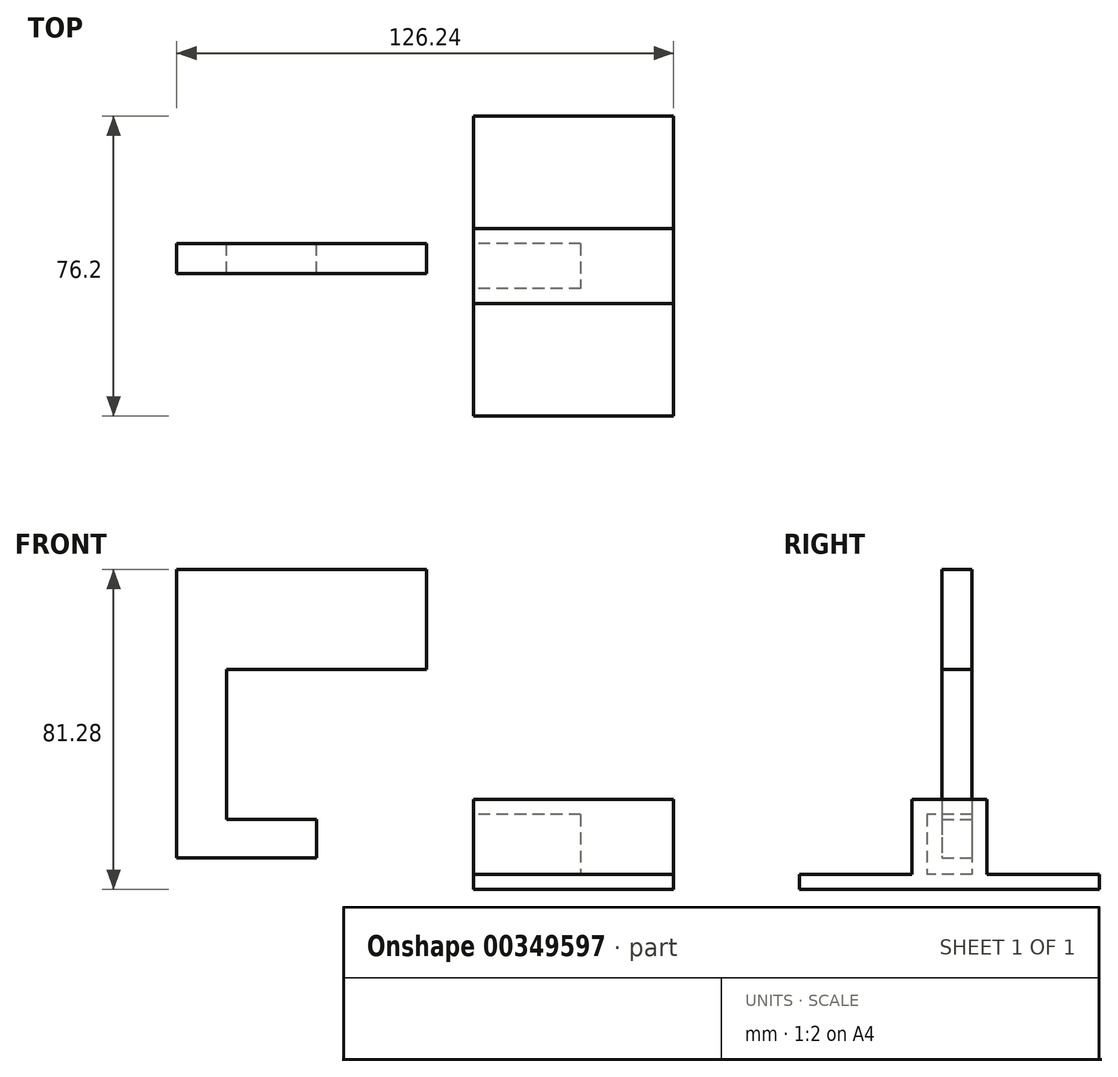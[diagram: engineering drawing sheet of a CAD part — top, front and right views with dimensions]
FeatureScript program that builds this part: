
annotation { "Feature Type Name" : "Feature", "Feature Type Description" : "" }
export const myFeature = defineFeature(function(context is Context, id is Id, definition is map)
    precondition{}
    {
        {
            var Q0;
            Q0=qCreatedBy(makeId("Top.planeOp"),FACE);
            var sketch = newSketch(context, id + "F0", { "sketchPlane" : qUnion([Q0])});
            skLineSegment(sketch, "E0.bottom", {"start": v(-61.72, 63.22) * mm, "end": v(-10.92, 63.22) * mm});
            skLineSegment(sketch, "E0.top", {"start": v(-61.72, -12.98) * mm, "end": v(-10.92, -12.98) * mm});
            skLineSegment(sketch, "E0.left", {"start": v(-61.72, 63.22) * mm, "end": v(-61.72, -12.98) * mm});
            skLineSegment(sketch, "E0.right", {"start": v(-10.92, 63.22) * mm, "end": v(-10.92, -12.98) * mm});
            skSolve(sketch);
        }
        {
            var Q0;
            Q0=makeQuery(id+"F0.imprint","IMPRINT",FACE,{"disambiguationData":[TD([[makeQuery(id+"F0.imprint","IMPRINT",EDGE,{"derivedFrom":sQuery(id+"F0.wireOp",EDGE,"E0.bottom")}),-1.0]])]});
            extrude(context, id + "F1", {"entities" : qUnion([Q0]), "depth" : 3.8 * mm, "offsetDistance" : 25.4 * mm});
        }
        {
            var Q0;
            Q0=makeQuery(id+"F1.opExtrude","CAP_FACE",FACE,{"disambiguationData":[OSD([sQuery(id+"F0.wireOp",EDGE,"E0.bottom"),sQuery(id+"F0.wireOp",EDGE,"E0.top"),sQuery(id+"F0.wireOp",EDGE,"E0.left"),sQuery(id+"F0.wireOp",EDGE,"E0.right")])],"isStart":false});
            var sketch = newSketch(context, id + "F2", { "sketchPlane" : qUnion([Q0])});
            skPoint(sketch, "E1", {"position": v(-61.72, 44.17) * mm});
            skPoint(sketch, "E2", {"position": v(-61.72, 6.07) * mm});
            skPoint(sketch, "E3", {"position": v(-10.92, 15.6) * mm});
            skPoint(sketch, "E4", {"position": v(-10.92, 34.64) * mm});
            skPoint(sketch, "E5", {"position": v(-61.72, 25.12) * mm});
            skPoint(sketch, "E6", {"position": v(-61.72, 34.64) * mm});
            skPoint(sketch, "E7", {"position": v(-61.72, 15.6) * mm});
            skLineSegment(sketch, "E8", {"start": v(-61.72, 34.64) * mm, "end": v(-10.92, 34.64) * mm});
            skLineSegment(sketch, "E9", {"start": v(-61.72, 15.6) * mm, "end": v(-10.92, 15.6) * mm});
            skLineSegment(sketch, "E10", {"start": v(-61.72, 34.64) * mm, "end": v(-61.72, 15.6) * mm});
            skLineSegment(sketch, "E11", {"start": v(-10.92, 34.64) * mm, "end": v(-10.92, 15.6) * mm});
            skSolve(sketch);
        }
        {
            var Q0;
            Q0=makeQuery(id+"F2.imprint","IMPRINT",FACE,{"disambiguationData":[TD([[makeQuery(id+"F2.imprint","IMPRINT",EDGE,{"derivedFrom":sQuery(id+"F2.wireOp",EDGE,"E8")}),-1.0]])]});
            extrude(context, id + "F3", {"entities" : qUnion([Q0]), "operationType" : NewBodyOperationType.ADD, "depth" : 19.05 * mm, "offsetDistance" : 25.4 * mm});
        }
        {
            var Q0;
            Q0=makeQuery(id+"F3.boolean.opBoolean","MERGE",FACE,{"derivedFrom":[makeQuery(id+"F1.opExtrude","SWEPT_FACE",FACE,{"disambiguationData":[OSD([sQuery(id+"F0.wireOp",EDGE,"E0.left")])]}),makeQuery(id+"F3.opExtrude","SWEPT_FACE",FACE,{"disambiguationData":[OSD([sQuery(id+"F2.wireOp",EDGE,"E10")])]})]});
            var sketch = newSketch(context, id + "F4", { "sketchPlane" : qUnion([Q0])});
            skPoint(sketch, "E12", {"position": v(-30.83, 22.86) * mm});
            skPoint(sketch, "E13", {"position": v(-19.4, 22.86) * mm});
            skPoint(sketch, "E14", {"position": v(-15.6, 7.62) * mm});
            skPoint(sketch, "E15", {"position": v(-34.64, 7.62) * mm});
            skLineSegment(sketch, "E16", {"start": v(-34.64, 3.81) * mm, "end": v(-15.6, 3.81) * mm});
            skLineSegment(sketch, "E17", {"start": v(-30.83, 22.86) * mm, "end": v(-30.83, 0) * mm});
            skLineSegment(sketch, "E18", {"start": v(-19.4, 22.86) * mm, "end": v(-19.4, 0) * mm});
            skPoint(sketch, "E19", {"position": v(-34.64, 19.05) * mm});
            skLineSegment(sketch, "E20", {"start": v(-34.64, 19.05) * mm, "end": v(-15.6, 19.05) * mm});
            skSolve(sketch);
        }
        {
            var Q0;
            {var subQ0=sQuery(id+"F4.wireOp",EDGE,"E20");var subQ1=sQuery(id+"F4.wireOp",EDGE,"E17");var subQ2=makeQuery(id+"F4.imprint","INTERSECT",VERTEX,{"derivedFrom":[subQ1,subQ0]});Q0=makeQuery(id+"F4.imprint","IMPRINT",FACE,{"disambiguationData":[TD([[makeQuery(id+"F4.imprint","IMPRINT",EDGE,{"disambiguationData":[TD([[subQ2,-1.0]])],"derivedFrom":subQ1}),1.0]])]});}
            extrude(context, id + "F5", {"entities" : qUnion([Q0]), "operationType" : NewBodyOperationType.REMOVE, "oppositeDirection" : true, "depth" : 27.18 * mm, "offsetDistance" : 25.4 * mm});
        }
        {
            var Q0;
            Q0=makeQuery(id+"F5.boolean.opBoolean","COPY",FACE,{"derivedFrom":makeQuery(id+"F5.opExtrude","SWEPT_FACE",FACE,{"disambiguationData":[OSD([sQuery(id+"F4.wireOp",EDGE,"E17")])]})});
            var sketch = newSketch(context, id + "F6", { "sketchPlane" : qUnion([Q0])});
            skLineSegment(sketch, "E21.bottom", {"start": v(-137.16, 17.78) * mm, "end": v(-101.6, 17.78) * mm});
            skLineSegment(sketch, "E21.top", {"start": v(-137.16, 7.98) * mm, "end": v(-101.6, 7.98) * mm});
            skLineSegment(sketch, "E21.left", {"start": v(-137.16, 17.78) * mm, "end": v(-137.16, 7.98) * mm});
            skLineSegment(sketch, "E21.right", {"start": v(-101.6, 17.78) * mm, "end": v(-101.6, 7.98) * mm});
            skSolve(sketch);
        }
        {
            var Q0;
            {var subQ0=sQuery(id+"F6.wireOp",EDGE,"E21.left");Q0=makeQuery(id+"F6.imprint","IMPRINT",FACE,{"disambiguationData":[TD([[makeQuery(id+"F6.imprint","IMPRINT",EDGE,{"derivedFrom":subQ0}),1.0]])]});}
            var Q1;
            {var subQ0=sQuery(id+"F6.wireOp",EDGE,"E21.right");Q1=makeQuery(id+"F6.imprint","IMPRINT",FACE,{"disambiguationData":[TD([[makeQuery(id+"F6.imprint","IMPRINT",EDGE,{"derivedFrom":subQ0}),-1.0]])]});}
            extrude(context, id + "F7", {"entities" : qUnion([Q0, Q1]), "operationType" : NewBodyOperationType.ADD, "depth" : 7.62 * mm, "offsetDistance" : 25.4 * mm});
        }
        {
            var Q0;
            Q0=makeQuery(id+"F7.opExtrude","SWEPT_FACE",FACE,{"disambiguationData":[OSD([sQuery(id+"F6.wireOp",EDGE,"E21.bottom")])]});
            var sketch = newSketch(context, id + "F8", { "sketchPlane" : qUnion([Q0])});
            skLineSegment(sketch, "E22.bottom", {"start": v(-137.16, 23.21) * mm, "end": v(-124.46, 23.21) * mm});
            skLineSegment(sketch, "E22.top", {"start": v(-137.16, 30.83) * mm, "end": v(-124.46, 30.83) * mm});
            skLineSegment(sketch, "E22.left", {"start": v(-137.16, 23.21) * mm, "end": v(-137.16, 30.83) * mm});
            skLineSegment(sketch, "E22.right", {"start": v(-124.46, 23.21) * mm, "end": v(-124.46, 30.83) * mm});
            skSolve(sketch);
        }
        {
            var Q0;
            Q0=makeQuery(id+"F8.imprint","IMPRINT",FACE,{"disambiguationData":[TD([[makeQuery(id+"F8.imprint","IMPRINT",EDGE,{"derivedFrom":sQuery(id+"F8.wireOp",EDGE,"E22.bottom")}),1.0]])]});
            extrude(context, id + "F9", {"entities" : qUnion([Q0]), "operationType" : NewBodyOperationType.ADD, "depth" : 63.5 * mm, "offsetDistance" : 25.4 * mm});
        }
        {
            var Q0;
            Q0=makeQuery(id+"F9.opExtrude","SWEPT_FACE",FACE,{"disambiguationData":[OSD([sQuery(id+"F8.wireOp",EDGE,"E22.right")])]});
            var sketch = newSketch(context, id + "F10", { "sketchPlane" : qUnion([Q0])});
            skLineSegment(sketch, "E23.bottom", {"start": v(23.21, 81.28) * mm, "end": v(30.83, 81.28) * mm});
            skLineSegment(sketch, "E23.top", {"start": v(23.21, 55.88) * mm, "end": v(30.83, 55.88) * mm});
            skLineSegment(sketch, "E23.left", {"start": v(23.21, 81.28) * mm, "end": v(23.21, 55.88) * mm});
            skLineSegment(sketch, "E23.right", {"start": v(30.83, 81.28) * mm, "end": v(30.83, 55.88) * mm});
            skSolve(sketch);
        }
        {
            var Q0;
            Q0=makeQuery(id+"F10.imprint","IMPRINT",FACE,{"disambiguationData":[TD([[makeQuery(id+"F10.imprint","IMPRINT",EDGE,{"derivedFrom":sQuery(id+"F10.wireOp",EDGE,"E23.bottom")}),-1.0]])]});
            extrude(context, id + "F11", {"entities" : qUnion([Q0]), "operationType" : NewBodyOperationType.ADD, "depth" : 50.8 * mm, "offsetDistance" : 25.4 * mm});
        }
    });
